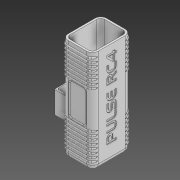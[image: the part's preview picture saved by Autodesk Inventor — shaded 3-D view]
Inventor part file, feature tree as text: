
AUTODESK INVENTOR PART (.ipt)
format: ipt  version: 2021 (Build 250183000, 183)  size: 2,071,552 bytes
history: native  units: mm
features: extrude x24, sketch x23, fillet x17, projected_geometry x10, plane x7, mirror x7, other x1
ambient origin geometry x8: Origin, YZ Plane, XZ Plane, XY Plane, X Axis, Y Axis, Z Axis, Center Point
bodies: Body1 (feature_tree)
feature tree (89):
  other  "Sólido1"
  extrude  "Extrusión1"  Depth=36.5mm
  extrude  "Extrusión2"  Depth=2.0mm
  extrude  "Extrusión3"  Depth=4.0mm
  plane  "Plano de trabajo1"
  mirror  "Simetría1"
  fillet  "Empalme1"  Radius=108.0mm
  plane  "Plano de trabajo2"
  extrude  "Extrusión4"  Depth=2.0mm
  plane  "Plano de trabajo3"
  mirror  "Simetría2"
  plane  "Plano de trabajo4"
  mirror  "Simetría3"
  plane  "Plano de trabajo5"
  mirror  "Simetría4"
  plane  "Plano de trabajo6"
  mirror  "Simetría5"
  plane  "Plano de trabajo8"
  mirror  "Simetría6"
  fillet  "Empalme2"  Radius=2.0mm
  fillet  "Empalme3"  Radius=2.0mm
  sketch  "Boceto4"  dims[d4=4.0mm d5=4.0mm d6=108.0mm d7=0.0mm]
  extrude  "Extrusión5"  Depth=2.0mm TaperAngle=0.0deg
  extrude  "Extrusión6"  Depth=6.0mm
  extrude  "Extrusión7"  Depth=11.0mm
  extrude  "Extrusión8"  [1 undecoded]
  extrude  "Extrusión9"  Depth=5.0mm
  extrude  "Extrusión10"  [1 undecoded]
  extrude  "Extrusión11"  [1 undecoded]
  extrude  "Extrusión12"  Depth=1.0mm
  extrude  "Extrusión13"  Depth=0.6mm TaperAngle=0.0deg
  extrude  "Extrusión14"  Depth=9.0mm
  extrude  "Extrusión15"  Depth=14.0mm TaperAngle=0.0deg
  extrude  "Extrusión16"  Depth=7.0mm
  fillet  "Empalme10"  Radius=1.8mm
  extrude  "Extrusión17"  Depth=2.0mm
  fillet  "Empalme13"  Radius=7.0mm
  fillet  "Empalme16"  Radius=6.0mm
  extrude  "Extrusión18"  Depth=8.0mm TaperAngle=0.0deg
  extrude  "Extrusión19"  Depth=10.0mm TaperAngle=0.0deg
  fillet  "Empalme20"  Radius=75.0mm
  fillet  "Empalme21"  Radius=75.0mm
  fillet  "Empalme22"  Radius=16.5mm
  fillet  "Empalme23"  Radius=11.273282mm
  fillet  "Empalme24"  Radius=5.0mm
  fillet  "Empalme25"  Radius=9.0mm
  fillet  "Empalme31"  Radius=9.0mm
  fillet  "Empalme32"  Radius=10.0mm
  extrude  "Extrusión20"  Depth=4.0mm
  fillet  "Empalme33"  Radius=6.0mm
  extrude  "Extrusión21"  Depth=2.0mm
  extrude  "Extrusión22"  Depth=2.0mm
  extrude  "Extrusión23"  Depth=0.5mm
  extrude  "Extrusión24"  Depth=0.5mm
  fillet  "Empalme34"  Radius=12.0mm
  fillet  "Empalme35"  Radius=1.5mm
  mirror  "Simetría8"
  sketch  "Boceto2"  dims[d0=27.85mm d1=36.5mm]
  sketch  "Boceto3"  dims[d2=2.0mm d3=6.0mm]
  sketch  "Boceto5"  dims[d8=2.0mm d9=0.0mm d10=8.0mm d11=2.0mm d12=2.0mm]
  sketch  "Boceto6"  dims[d13=2.0mm d14=2.0mm d15=0.0mm]
  sketch  "Boceto7"  dims[d16=20.0mm d17=6.0mm]
  sketch  "Boceto8"  dims[d18=3.2mm d19=11.0mm]
  projected_geometry  "Contorno proyectado1"
  sketch  "Boceto9"  dims[d20=5.0mm d21=-4.0mm]
  sketch  "Boceto10"  dims[d22=0.8mm d23=5.0mm]
  sketch  "Boceto11"  dims[d24=2.0mm d25=0.0mm d26=-3.0mm]
  sketch  "Boceto12"  dims[d27=-4.0mm d28=-8.0mm]
  sketch  "Boceto13"  dims[d29=-33.5mm d30=1.0mm]
  projected_geometry  "Contorno proyectado2"
  sketch  "Boceto14"  dims[d31=1.0mm d32=0.6mm d33=0.0mm]
  sketch  "Boceto18"  dims[d37=20.0mm d39=9.0mm]
  sketch  "Boceto19"  dims[d40=24.0mm d41=14.0mm d42=0.0mm]
  projected_geometry  "Contorno proyectado7"
  sketch  "Boceto20"  dims[d43=8.0mm d44=0.0mm d45=7.0mm d46=1.8mm]
  sketch  "Boceto21"  dims[d47=15.0mm d48=0.0mm d49=2.0mm d50=7.0mm d51=0.0mm d53=6.0mm d54=0.0mm]
  sketch  "Boceto22"  dims[d56=14.0mm d57=0.0mm d58=8.0mm d59=0.0mm]
  sketch  "Boceto24"  dims[d60=8.0mm d61=0.0mm d63=8.0mm d64=0.0mm d65=75.0mm d66=75.0mm d67=16.5mm d68=11.273282mm d70=5.0mm d72=9.0mm d73=9.0mm d75=10.0mm d76=0.0mm]
  projected_geometry  "Contorno proyectado9"
  sketch  "Boceto25"  dims[d78=6.0mm d79=4.0mm d80=6.0mm]
  sketch  "Boceto26"  dims[d81=2.0mm d82=2.0mm]
  projected_geometry  "Contorno proyectado10"
  projected_geometry  "Contorno proyectado11"
  sketch  "Boceto27"  dims[d83=0.5mm d84=0.0mm d85=2.0mm]
  projected_geometry  "Contorno proyectado12"
  projected_geometry  "Contorno proyectado13"
  sketch  "Boceto28"  dims[d88=0.5mm d89=0.0mm d90=1.5mm d93=4.0mm d96=12.0mm d97=1.5mm d98=1.653837mm d99=10.0mm d100=0.0mm d101=10.0mm d102=0.0mm d104=1.5mm d105=1.5mm d106=1.5mm d107=1.5mm d108=0.5mm d109=0.5mm d115=1.0mm d116=5.0mm d117=1.0mm d118=10.0mm d119=0.0mm d120=0.2mm d122=16.9mm d123=10.0mm d124=0.0mm d125=10.0mm d126=0.0mm d127=9.0mm d128=0.0mm d129=9.0mm d130=0.0mm d131=2.0mm d132=2.0mm d74=0.5mm d77=0.872665mm]
  projected_geometry  "Contorno proyectado14"
  projected_geometry  "Contorno proyectado15"
note: 3 required parameter values undecoded (feature->parameter linkage not recoverable at this tier; creation-order binding heuristic only, values carry confidence <= 0.55)
